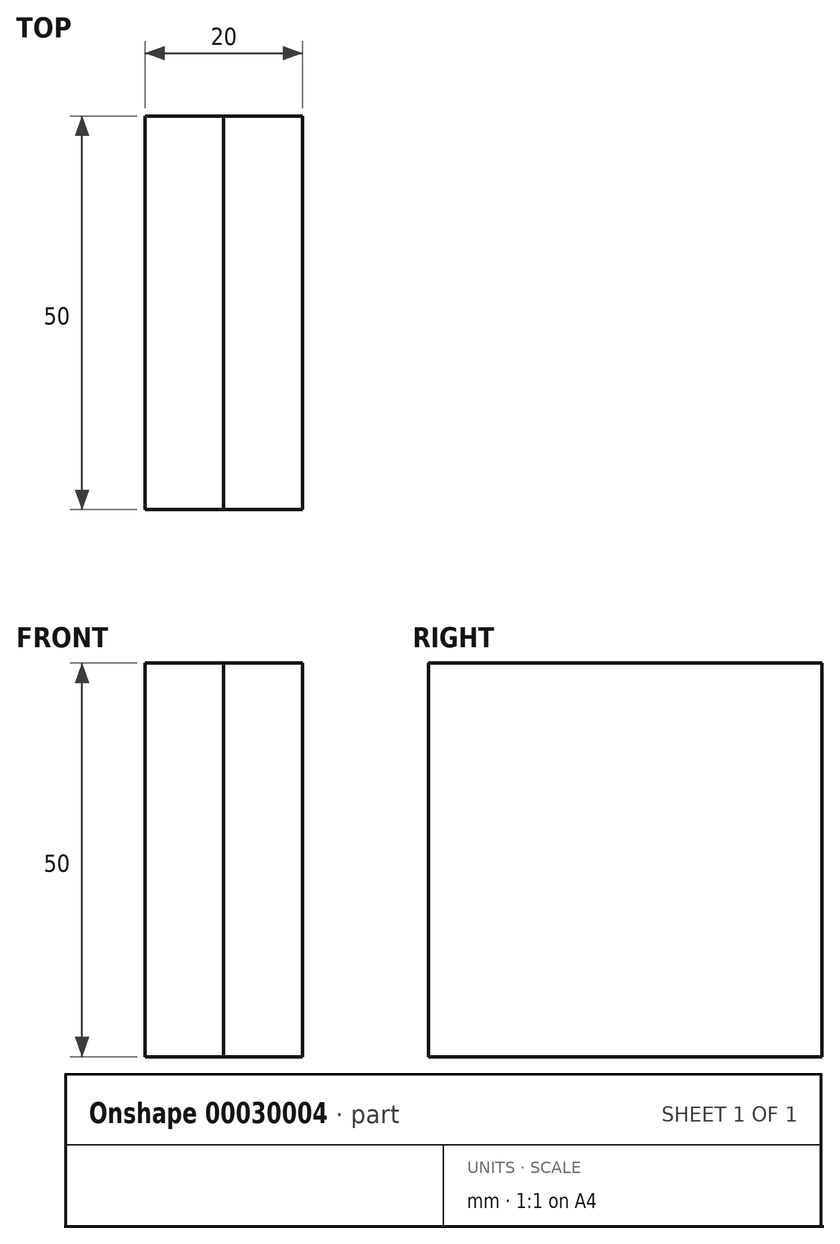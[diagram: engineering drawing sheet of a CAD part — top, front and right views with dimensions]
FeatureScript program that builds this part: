
annotation { "Feature Type Name" : "Feature", "Feature Type Description" : "" }
export const myFeature = defineFeature(function(context is Context, id is Id, definition is map)
    precondition{}
    {
        {
            var Q0;
            Q0=qCreatedBy(makeId("Right.planeOp"),FACE);
            var sketch = newSketch(context, id + "F0", { "sketchPlane" : qUnion([Q0])});
            skLineSegment(sketch, "E0.bottom", {"start": v(0, 0) * mm, "end": v(-50, 0) * mm});
            skLineSegment(sketch, "E0.top", {"start": v(0, -50) * mm, "end": v(-50, -50) * mm});
            skLineSegment(sketch, "E0.left", {"start": v(0, 0) * mm, "end": v(0, -50) * mm});
            skLineSegment(sketch, "E0.right", {"start": v(-50, 0) * mm, "end": v(-50, -50) * mm});
            skSolve(sketch);
        }
        {
            var Q0;
            Q0 = qSketchRegion(id + "F0", true);
            extrude(context, id + "F1", {"entities" : qUnion([Q0]), "depth" : 10 * mm});
        }
        {
            var Q0;
            Q0=makeQuery(id+"F1.opExtrude","CAP_FACE",FACE,{"disambiguationData":[OSD([sQuery(id+"F0.wireOp",EDGE,"E0.bottom"),sQuery(id+"F0.wireOp",EDGE,"E0.top"),sQuery(id+"F0.wireOp",EDGE,"E0.left"),sQuery(id+"F0.wireOp",EDGE,"E0.right")])],"isStart":true});
            var sketch = newSketch(context, id + "F2", { "sketchPlane" : qUnion([Q0])});
            skLineSegment(sketch, "E1.bottom", {"start": v(0, 0) * mm, "end": v(50, 0) * mm});
            skLineSegment(sketch, "E1.top", {"start": v(0, -50) * mm, "end": v(50, -50) * mm});
            skLineSegment(sketch, "E1.left", {"start": v(0, 0) * mm, "end": v(0, -50) * mm});
            skLineSegment(sketch, "E1.right", {"start": v(50, 0) * mm, "end": v(50, -50) * mm});
            skSolve(sketch);
        }
        {
            var Q0;
            Q0 = qSketchRegion(id + "F2", true);
            extrude(context, id + "F3", {"entities" : qUnion([Q0]), "depth" : 10 * mm});
        }
    });
